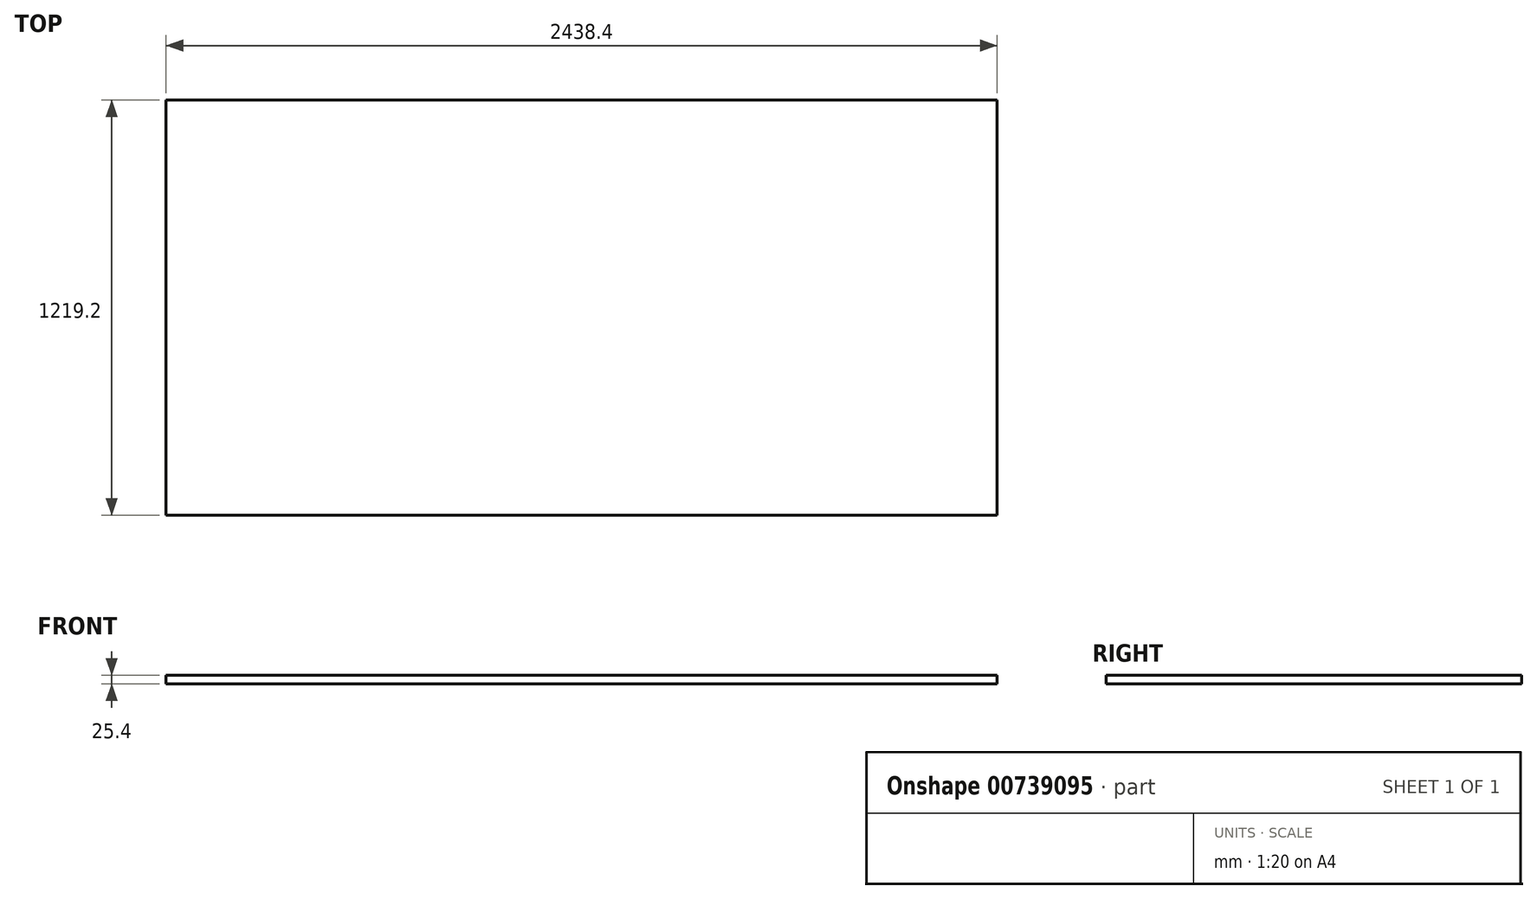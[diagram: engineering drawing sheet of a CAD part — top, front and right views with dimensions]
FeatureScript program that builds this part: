
annotation { "Feature Type Name" : "Feature", "Feature Type Description" : "" }
export const myFeature = defineFeature(function(context is Context, id is Id, definition is map)
    precondition{}
    {
        {
            var Q0;
            Q0=qCreatedBy(makeId("Top.planeOp"),FACE);
            var sketch = newSketch(context, id + "F0", { "sketchPlane" : qUnion([Q0])});
            skLineSegment(sketch, "E0.bottom", {"start": v(0, 0) * mm, "end": v(2438.4, 0) * mm});
            skLineSegment(sketch, "E0.top", {"start": v(0, 1219.2) * mm, "end": v(2438.4, 1219.2) * mm});
            skLineSegment(sketch, "E0.left", {"start": v(0, 0) * mm, "end": v(0, 1219.2) * mm});
            skLineSegment(sketch, "E0.right", {"start": v(2438.4, 0) * mm, "end": v(2438.4, 1219.2) * mm});
            skSolve(sketch);
        }
        {
            var Q0;
            Q0=makeQuery(id+"F0.imprint","IMPRINT",FACE,{"disambiguationData":[TD([[makeQuery(id+"F0.imprint","IMPRINT",EDGE,{"derivedFrom":sQuery(id+"F0.wireOp",EDGE,"E0.bottom")}),1.0]])]});
            extrude(context, id + "F1", {"entities" : qUnion([Q0]), "depth" : 25.4 * mm, "offsetDistance" : 25.4 * mm});
        }
    });
